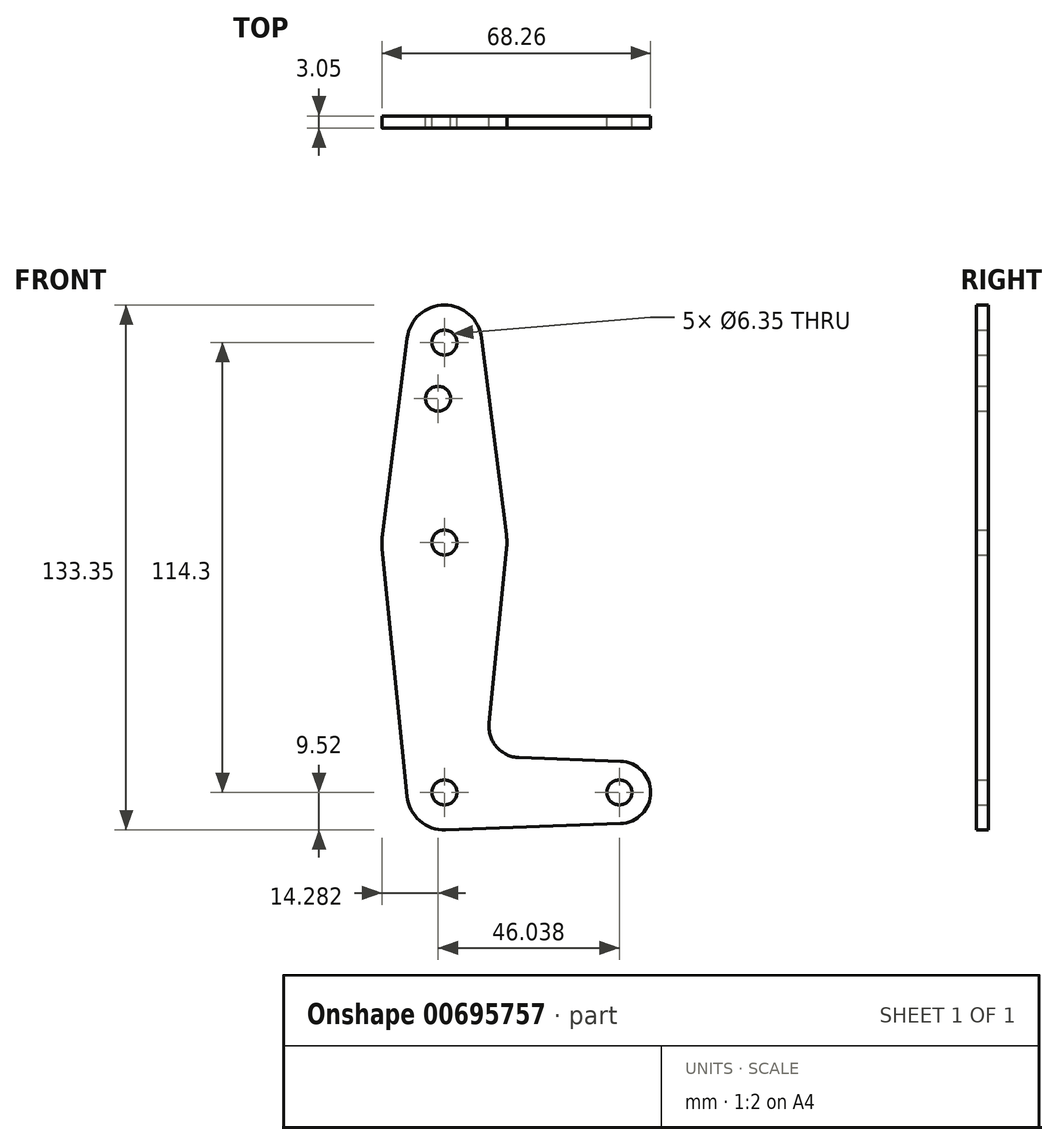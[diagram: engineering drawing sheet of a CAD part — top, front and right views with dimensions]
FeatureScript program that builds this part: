
annotation { "Feature Type Name" : "Feature", "Feature Type Description" : "" }
export const myFeature = defineFeature(function(context is Context, id is Id, definition is map)
    precondition{}
    {
        {
            var Q0;
            Q0=qCreatedBy(makeId("Front.planeOp"),FACE);
            var sketch = newSketch(context, id + "F0", { "sketchPlane" : qUnion([Q0])});
            skCircle(sketch, "E0", {"center": v(0, 0) * mm, "radius": 9.53 * mm});
            skLineSegment(sketch, "E1", {"start": v(0, 0) * mm, "end": v(0, 114.3) * mm, "construction": true});
            skCircle(sketch, "E2", {"center": v(0, 114.3) * mm, "radius": 9.53 * mm});
            skCircle(sketch, "E3", {"center": v(0, 63.5) * mm, "radius": 15.88 * mm});
            skLineSegment(sketch, "E4", {"start": v(0, 0) * mm, "end": v(44.45, 0) * mm, "construction": true});
            skCircle(sketch, "E5", {"center": v(44.45, 0) * mm, "radius": 7.94 * mm});
            skLineSegment(sketch, "E6", {"start": v(-9.45, 115.5) * mm, "end": v(-15.75, 65.48) * mm});
            skLineSegment(sketch, "E7", {"start": v(-15.8, 61.91) * mm, "end": v(-9.48, -0.95) * mm});
            skLineSegment(sketch, "E8", {"start": v(9.45, 115.5) * mm, "end": v(15.75, 65.48) * mm});
            skLineSegment(sketch, "E9", {"start": v(15.8, 61.91) * mm, "end": v(11.34, 17.6) * mm});
            skLineSegment(sketch, "E10", {"start": v(18.97, 8.85) * mm, "end": v(44.73, 7.93) * mm});
            skLineSegment(sketch, "E11", {"start": v(0.34, -9.52) * mm, "end": v(44.73, -7.93) * mm});
            skCircle(sketch, "E12", {"center": v(0, 114.3) * mm, "radius": 3.18 * mm});
            skCircle(sketch, "E13", {"center": v(0, 63.5) * mm, "radius": 3.18 * mm});
            skCircle(sketch, "E14", {"center": v(0, 0) * mm, "radius": 3.18 * mm});
            skCircle(sketch, "E15", {"center": v(44.45, 0) * mm, "radius": 3.18 * mm});
            skCircle(sketch, "E16", {"center": v(-1.59, 100.03) * mm, "radius": 3.18 * mm});
            skArc(sketch, "E17.filletArc", {"start": v(11.34, 17.6) * mm, "mid": v(13.26, 11.57) * mm, "end": v(18.97, 8.85) * mm});
            skSolve(sketch);
        }
        {
            var Q0;
            Q0 = qSketchRegion(id + "F0", true);
            extrude(context, id + "F1", {"entities" : qUnion([Q0]), "depth" : 3.05 * mm, "offsetDistance" : 25.4 * mm});
        }
    });
